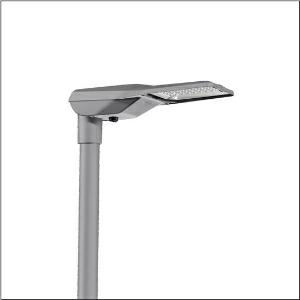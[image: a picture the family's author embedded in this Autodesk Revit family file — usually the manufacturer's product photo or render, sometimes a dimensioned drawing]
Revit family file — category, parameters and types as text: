
# Revit family: streetlight_sl_21_iq_mini___st1_0a_5xe2d31u08hb_e98e
name_source: partatom
category: Lighting Fixtures
units: mm (PartAtom-declared; Revit-internal decimal feet)

## family parameters
Cut with Voids When Loaded = No
Host = Face
Light Source = No
Part Type = Normal
Room Calculation Point = No
Round Connector Dimension = Use Diameter
Shared = No

## types (1)
- --- (1 x LED, 9750 lm, 71 W, 3000K)
    Apparent Load = 71 VA
    CIE Flux Codes = 37 72 97 100 100
    Color Rendering = 70
    Color Temperature = 3000K
    Default Elevation = 1800 mm
    Description = Streetlight SL 21 iQ mini, mast luminaire, primary light control with lens, of PMMA, primary optical cover: cover, of toughened safety glass, transparent, light distribution: ST1.0a, light emission: direct distribution, primary light characteristic: asymmetric, installation type: post-top, side-entry, LED, High Power LED, rated luminous flux: 9.750lm, luminous efficacy: 137lm/W, light colour: 730, colour temperature: 3000K, control: presetting dimming logarithmic, Street-Remote, Auto-Match, Temp-Guard, Lumen-Switch, Night-Set, Smart-Wire, Light-Fading, Desk-Remote (wireless, voltage-free reading and setting of iQ features in the workshop via application-optimized NFC function/RFID function), optimised constant luminous flux control (CLO 2.0), mains connection: 220..240V, AC, 50/60Hz, start of lifetime: 71W, end of service life: 75W, reduction: 30W, luminaire housing, of diecast aluminium, powder-coated, Siteco® metallic grey (DB 702S), corrosivity category C5 mid according to DIN EN ISO 12944, please order mast flange separately, inclination adjustable: 0°, 5°, 10°, 15°, sealing non-destructively replaceable, multi-level sealing system, length: 628mm, width: 235mm, height: 110mm, mast flange for spigot size: 42mm (side-entry): 5XC10008XM4, 60/48mm (side-entry/post-top): 5XC10108XM2, 76/60mm (side-entry/post-top): 5XC10108XM1, Smart Interface below, protection rating (complete): IP66, insulation class (complete): insulation class II (safety insulation), certification: CE, ENEC, ENEC+, VDE, impact resistance: IK09, permissible operating ambient temperature for outdoor applications: -40..+50°C, standard-compliant lighting for roads and squares, packaging unit: 1 piece

Light Distribution: ST1.0a
    Height = 110 mm
    Lamp = 1 x LED
    Lamp Light Flux = 9750 lm
    Lamp Power = 71 W
    Lamp count = 1
    Length = 625 mm
    Luminous efficacy = 137 lm/W
    Manufacturer = Siteco
    ModVariant = No
    Model = 5XE2D31U08HB
    Number of Poles = 1
    OnlyDefault = Yes
    Power Factor = 1
    Product Name = Streetlight SL 21 iQ mini | ST1.0a
    Product group = mast luminaire | pylon top
    ProductGroupID = 6100
    Protection Class = Protection class II
    Protection Degree = IP 66
    RLX_Detail_Level = 1
    RLX_Emergency_Light_Flux = 0 lm
    RLX_Emergency_Type = 0
    RLX_Emergency_Type_DB = No
    RlxData = <blob elided: 92213 chars, md5=5d50ae53>
    Socket = socket
    Standby Power = 0 W
    System Light Flux = 9750 lm
    System Power = 71 W
    Type Comments = factory setting: luminous flux: 100 % | dim-lin: 254 | 716 mA
    Type Image = l_1003516.jpg
    URL = http://relux.com
    VarID = @adj_045227
    Voltage = 0 V
    Weight = 0.00 kg
    Width = 234 mm

## geometry (parser evidence)
native form markers: Blend x4, Sweep x9
no freeform markers — native parametric forms only
